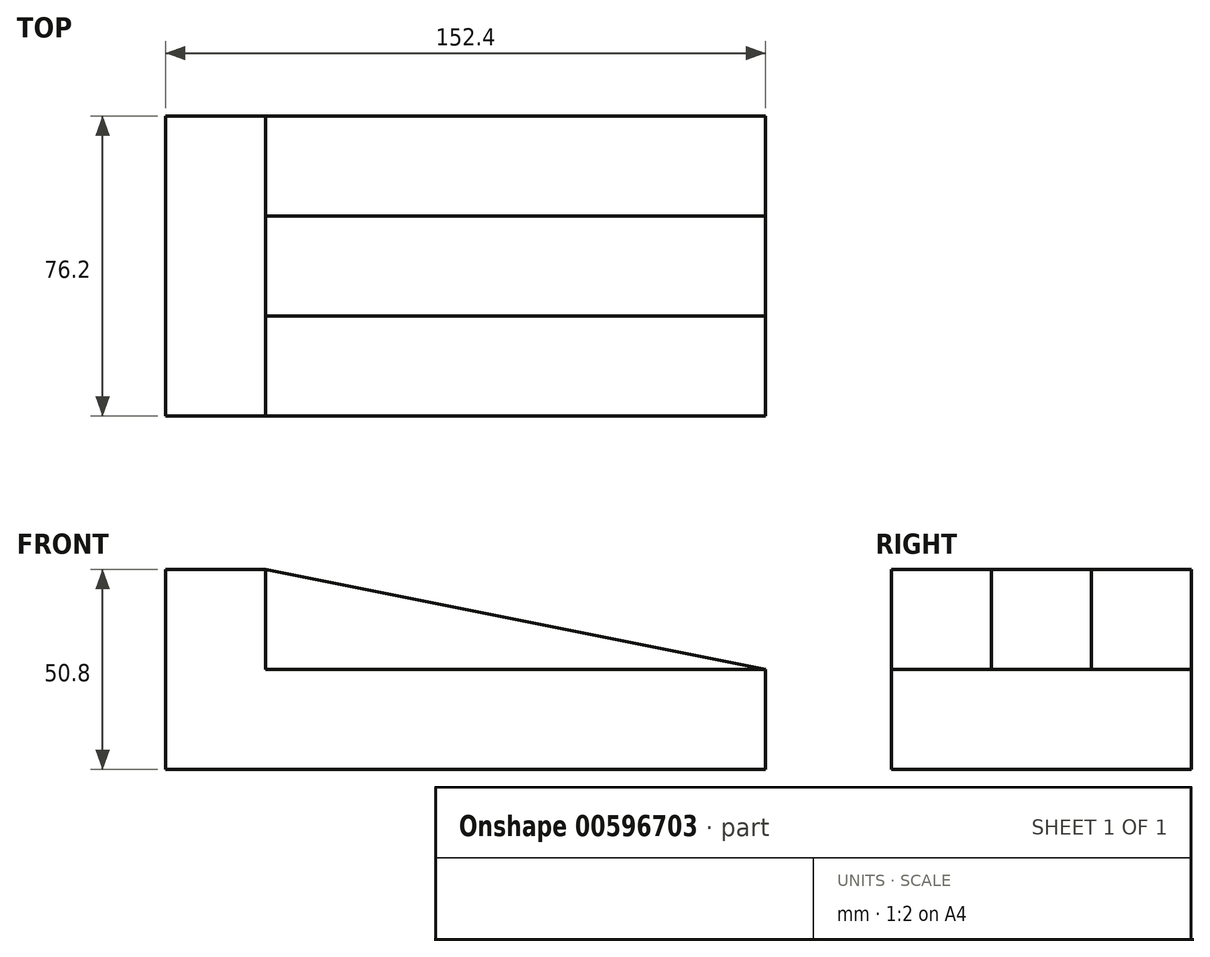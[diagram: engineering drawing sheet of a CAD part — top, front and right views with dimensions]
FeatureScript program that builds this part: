
annotation { "Feature Type Name" : "Feature", "Feature Type Description" : "" }
export const myFeature = defineFeature(function(context is Context, id is Id, definition is map)
    precondition{}
    {
        {
            var Q0;
            Q0=qCreatedBy(makeId("Right.planeOp"),FACE);
            var sketch = newSketch(context, id + "F0", { "sketchPlane" : qUnion([Q0])});
            skLineSegment(sketch, "E0", {"start": v(0, 67.48) * mm, "end": v(76.2, 67.48) * mm});
            skLineSegment(sketch, "E1", {"start": v(76.2, 67.48) * mm, "end": v(76.2, 118.28) * mm});
            skLineSegment(sketch, "E2", {"start": v(76.2, 118.28) * mm, "end": v(0, 118.28) * mm});
            skLineSegment(sketch, "E3", {"start": v(0, 118.28) * mm, "end": v(0, 67.48) * mm});
            skSolve(sketch);
        }
        {
            var Q0;
            Q0=makeQuery(id+"F0.imprint","IMPRINT",FACE,{"disambiguationData":[TD([[makeQuery(id+"F0.imprint","IMPRINT",EDGE,{"derivedFrom":sQuery(id+"F0.wireOp",EDGE,"E0")}),1.0]])]});
            extrude(context, id + "F1", {"entities" : qUnion([Q0]), "depth" : 152.4 * mm, "offsetDistance" : 25.4 * mm});
        }
        {
            var Q0;
            Q0=makeQuery(id+"F1.opExtrude","SWEPT_FACE",FACE,{"disambiguationData":[OSD([sQuery(id+"F0.wireOp",EDGE,"E1")])]});
            var sketch = newSketch(context, id + "F2", { "sketchPlane" : qUnion([Q0])});
            skLineSegment(sketch, "E4", {"start": v(0, 118.28) * mm, "end": v(-25.4, 118.28) * mm});
            skLineSegment(sketch, "E5", {"start": v(-25.4, 118.28) * mm, "end": v(-152.4, 92.88) * mm});
            skLineSegment(sketch, "E6", {"start": v(-152.4, 92.88) * mm, "end": v(0, 92.88) * mm});
            skLineSegment(sketch, "E7", {"start": v(0, 92.88) * mm, "end": v(-25.4, 92.88) * mm});
            skLineSegment(sketch, "E8", {"start": v(-25.4, 92.88) * mm, "end": v(-25.4, 118.28) * mm});
            skSolve(sketch);
        }
        {
            var Q0;
            {var subQ0=sQuery(id+"F2.wireOp",EDGE,"E5");Q0=makeQuery(id+"F2.imprint","IMPRINT",FACE,{"disambiguationData":[TD([[makeQuery(id+"F2.imprint","IMPRINT",EDGE,{"derivedFrom":subQ0}),-1.0]])]});}
            extrude(context, id + "F3", {"entities" : qUnion([Q0]), "operationType" : NewBodyOperationType.REMOVE, "oppositeDirection" : true, "depth" : 76.2 * mm, "offsetDistance" : 25.4 * mm});
        }
        {
            var Q0;
            Q0=makeQuery(id+"F1.opExtrude","SWEPT_FACE",FACE,{"disambiguationData":[OSD([sQuery(id+"F0.wireOp",EDGE,"E1")])]});
            var sketch = newSketch(context, id + "F4", { "sketchPlane" : qUnion([Q0])});
            skLineSegment(sketch, "E9", {"start": v(-25.4, 118.28) * mm, "end": v(-25.4, 92.88) * mm});
            skLineSegment(sketch, "E10", {"start": v(-25.4, 92.88) * mm, "end": v(-152.4, 92.88) * mm});
            skSolve(sketch);
        }
        {
            var Q0;
            Q0 = qSketchRegion(id + "F4", true);
            var Q1;
            Q1=makeQuery(id+"F4.imprint","IMPRINT",FACE,{"disambiguationData":[TD([[makeQuery(id+"F4.imprint","IMPRINT",EDGE,{"derivedFrom":sQuery(id+"F4.wireOp",EDGE,"E9")}),-1.0]])]});
            extrude(context, id + "F5", {"entities" : qUnion([Q0, Q1]), "operationType" : NewBodyOperationType.REMOVE, "oppositeDirection" : true, "depth" : 25.4 * mm, "offsetDistance" : 25.4 * mm});
        }
        {
            var Q0;
            Q0=makeQuery(id+"F1.opExtrude","SWEPT_FACE",FACE,{"disambiguationData":[OSD([sQuery(id+"F0.wireOp",EDGE,"E3")])]});
            var sketch = newSketch(context, id + "F6", { "sketchPlane" : qUnion([Q0])});
            skLineSegment(sketch, "E11", {"start": v(25.4, 118.28) * mm, "end": v(25.4, 92.88) * mm});
            skLineSegment(sketch, "E12", {"start": v(25.4, 92.88) * mm, "end": v(152.4, 92.88) * mm});
            skSolve(sketch);
        }
        {
            var Q0;
            Q0 = qSketchRegion(id + "F6", true);
            var Q1;
            Q1=makeQuery(id+"F6.imprint","IMPRINT",FACE,{"disambiguationData":[TD([[makeQuery(id+"F6.imprint","IMPRINT",EDGE,{"derivedFrom":sQuery(id+"F6.wireOp",EDGE,"E11")}),1.0]])]});
            extrude(context, id + "F7", {"entities" : qUnion([Q0, Q1]), "operationType" : NewBodyOperationType.REMOVE, "oppositeDirection" : true, "depth" : 25.4 * mm, "offsetDistance" : 25.4 * mm});
        }
    });
